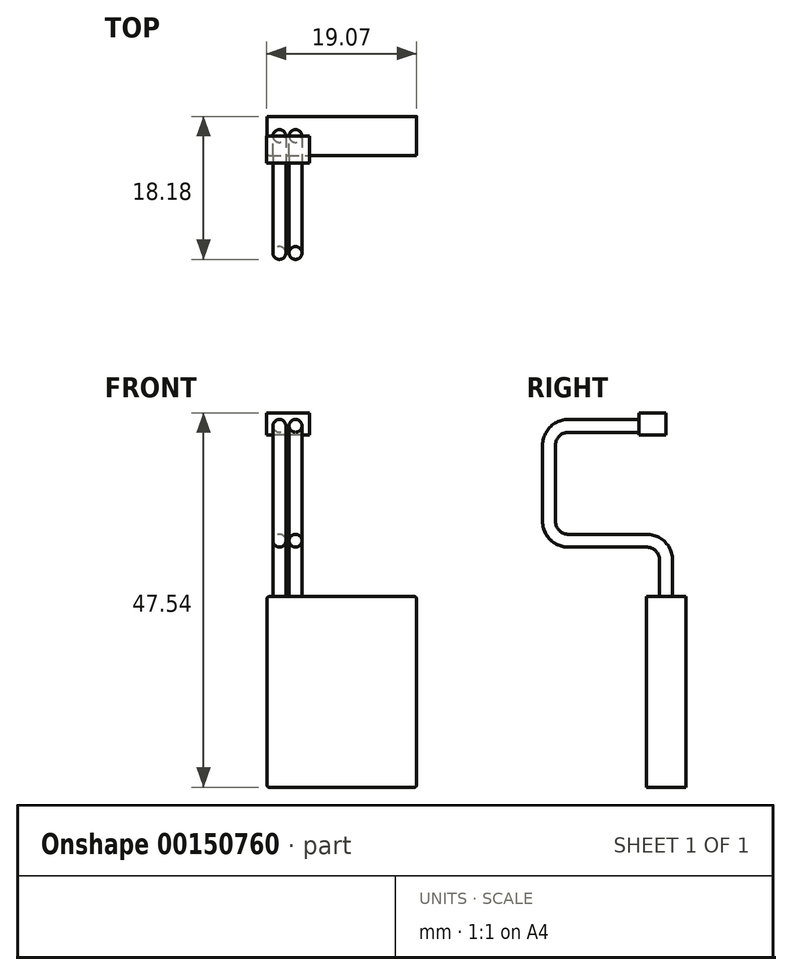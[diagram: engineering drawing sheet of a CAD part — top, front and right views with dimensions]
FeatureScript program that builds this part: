
annotation { "Feature Type Name" : "Feature", "Feature Type Description" : "" }
export const myFeature = defineFeature(function(context is Context, id is Id, definition is map)
    precondition{}
    {
        {
            var Q0;
            Q0=qCreatedBy(makeId("Front.planeOp"),FACE);
            var sketch = newSketch(context, id + "F0", { "sketchPlane" : qUnion([Q0])});
            skLineSegment(sketch, "E0.bottom", {"start": v(-9.25, -11.28) * mm, "end": v(9.75, -11.28) * mm});
            skLineSegment(sketch, "E0.top", {"start": v(-9.25, 12.92) * mm, "end": v(9.75, 12.92) * mm});
            skLineSegment(sketch, "E0.left", {"start": v(-9.25, -11.28) * mm, "end": v(-9.25, 12.92) * mm});
            skLineSegment(sketch, "E0.right", {"start": v(9.75, -11.28) * mm, "end": v(9.75, 12.92) * mm});
            skSolve(sketch);
        }
        {
            var Q0;
            Q0=makeQuery(id+"F0.imprint","IMPRINT",FACE,{"disambiguationData":[TD([[makeQuery(id+"F0.imprint","IMPRINT",EDGE,{"derivedFrom":sQuery(id+"F0.wireOp",EDGE,"E0.bottom")}),1.0]])]});
            extrude(context, id + "F1", {"entities" : qUnion([Q0]), "endBound" : BoundingType.SYMMETRIC, "depth" : 5 * mm});
        }
        {
            var Q0;
            Q0=makeQuery(id+"F1.opExtrude","SWEPT_EDGE",EDGE,{"disambiguationData":[OSD([sQuery(id+"F0.wireOp",EDGE,"E0.top"),sQuery(id+"F0.wireOp",EDGE,"E0.right")])]});
            var Q1;
            Q1=makeQuery(id+"F1.opExtrude","SWEPT_EDGE",EDGE,{"disambiguationData":[OSD([sQuery(id+"F0.wireOp",EDGE,"E0.top"),sQuery(id+"F0.wireOp",EDGE,"E0.left")])]});
            var Q2;
            Q2=makeQuery(id+"F1.opExtrude","SWEPT_EDGE",EDGE,{"disambiguationData":[OSD([sQuery(id+"F0.wireOp",EDGE,"E0.bottom"),sQuery(id+"F0.wireOp",EDGE,"E0.left")])]});
            var Q3;
            Q3=makeQuery(id+"F1.opExtrude","SWEPT_EDGE",EDGE,{"disambiguationData":[OSD([sQuery(id+"F0.wireOp",EDGE,"E0.bottom"),sQuery(id+"F0.wireOp",EDGE,"E0.right")])]});
            fillet(context, id + "F2", {"entities" : qUnion([Q0, Q1, Q2, Q3]), "radius" : 0.25 * mm, "tangentPropagation" : true, "allowEdgeOverflow" : false});
        }
        {
            var Q0;
            Q0=qCreatedBy(makeId("Right.planeOp"),FACE);
            var sketch = newSketch(context, id + "F3", { "sketchPlane" : qUnion([Q0])});
            skLineSegment(sketch, "E1", {"start": v(0, 12.92) * mm, "end": v(0, 17.57) * mm});
            skArc(sketch, "E2", {"start": v(0, 17.57) * mm, "mid": v(-0.72, 19.31) * mm, "end": v(-2.46, 20.03) * mm});
            skLineSegment(sketch, "E3", {"start": v(-2.46, 20.03) * mm, "end": v(-12.4, 20.03) * mm});
            skArc(sketch, "E4", {"start": v(-14.86, 22.5) * mm, "mid": v(-14.14, 20.75) * mm, "end": v(-12.4, 20.03) * mm});
            skLineSegment(sketch, "E5", {"start": v(-14.86, 22.5) * mm, "end": v(-14.86, 32.16) * mm});
            skArc(sketch, "E6", {"start": v(-12.4, 34.62) * mm, "mid": v(-14.14, 33.9) * mm, "end": v(-14.86, 32.16) * mm});
            skLineSegment(sketch, "E7", {"start": v(-12.4, 34.62) * mm, "end": v(-3.47, 34.62) * mm});
            skSolve(sketch);
        }
        {
            var Q0;
            Q0=makeQuery(id+"F1.opExtrude","SWEPT_FACE",FACE,{"disambiguationData":[OSD([sQuery(id+"F0.wireOp",EDGE,"E0.top")])]});
            var sketch = newSketch(context, id + "F4", { "sketchPlane" : qUnion([Q0])});
            skCircle(sketch, "E8", {"center": v(-7.68, 0) * mm, "radius": 0.82 * mm});
            skCircle(sketch, "E9", {"center": v(-5.64, 0) * mm, "radius": 0.82 * mm});
            skSolve(sketch);
        }
        {
            var Q0;
            Q0=makeQuery(id+"F4.imprint","IMPRINT",FACE,{"disambiguationData":[TD([[makeQuery(id+"F4.imprint","IMPRINT",EDGE,{"derivedFrom":sQuery(id+"F4.wireOp",EDGE,"E9")}),1.0]])]});
            var Q1;
            Q1=makeQuery(id+"F4.imprint","IMPRINT",FACE,{"disambiguationData":[TD([[makeQuery(id+"F4.imprint","IMPRINT",EDGE,{"derivedFrom":sQuery(id+"F4.wireOp",EDGE,"E8")}),1.0]])]});
            var Q2;
            Q2=sQuery(id+"F3.wireOp",EDGE,"E1");
            var Q3;
            Q3=sQuery(id+"F3.wireOp",EDGE,"E2");
            var Q4;
            Q4=sQuery(id+"F3.wireOp",EDGE,"E3");
            var Q5;
            Q5=sQuery(id+"F3.wireOp",EDGE,"E4");
            var Q6;
            Q6=sQuery(id+"F3.wireOp",EDGE,"E5");
            var Q7;
            Q7=sQuery(id+"F3.wireOp",EDGE,"E6");
            var Q8;
            Q8=sQuery(id+"F3.wireOp",EDGE,"E7");
            sweep(context, id + "F5", {"operationType" : NewBodyOperationType.ADD, "profiles" : qUnion([Q0, Q1]), "path" : qUnion([Q2, Q3, Q4, Q5, Q6, Q7, Q8])});
        }
        {
            var Q0;
            Q0=qCreatedBy(makeId("Front.planeOp"),FACE);
            var sketch = newSketch(context, id + "F6", { "sketchPlane" : qUnion([Q0])});
            skLineSegment(sketch, "E10.bottom", {"start": v(-9.32, 36.26) * mm, "end": v(-3.85, 36.26) * mm});
            skLineSegment(sketch, "E10.top", {"start": v(-9.32, 33.44) * mm, "end": v(-3.85, 33.44) * mm});
            skLineSegment(sketch, "E10.left", {"start": v(-9.32, 36.26) * mm, "end": v(-9.32, 33.44) * mm});
            skLineSegment(sketch, "E10.right", {"start": v(-3.85, 36.26) * mm, "end": v(-3.85, 33.44) * mm});
            skSolve(sketch);
        }
        {
            var Q0;
            Q0=makeQuery(id+"F6.imprint","IMPRINT",FACE,{"disambiguationData":[TD([[makeQuery(id+"F6.imprint","IMPRINT",EDGE,{"derivedFrom":sQuery(id+"F6.wireOp",EDGE,"E10.bottom")}),-1.0]])]});
            var Q1;
            Q1=makeQuery(id+"F5.opSweep","CAP_FACE",FACE,{"disambiguationData":[OSD([sQuery(id+"F3.wireOp",VERTEX,"E7.end"),sQuery(id+"F4.wireOp",EDGE,"E8")])],"isStart":false});
            extrude(context, id + "F7", {"entities" : qUnion([Q0]), "operationType" : NewBodyOperationType.ADD, "endBound" : BoundingType.UP_TO_SURFACE, "endBoundEntityFace" : qUnion([Q1]), "depth" : 25.4 * mm});
        }
    });
